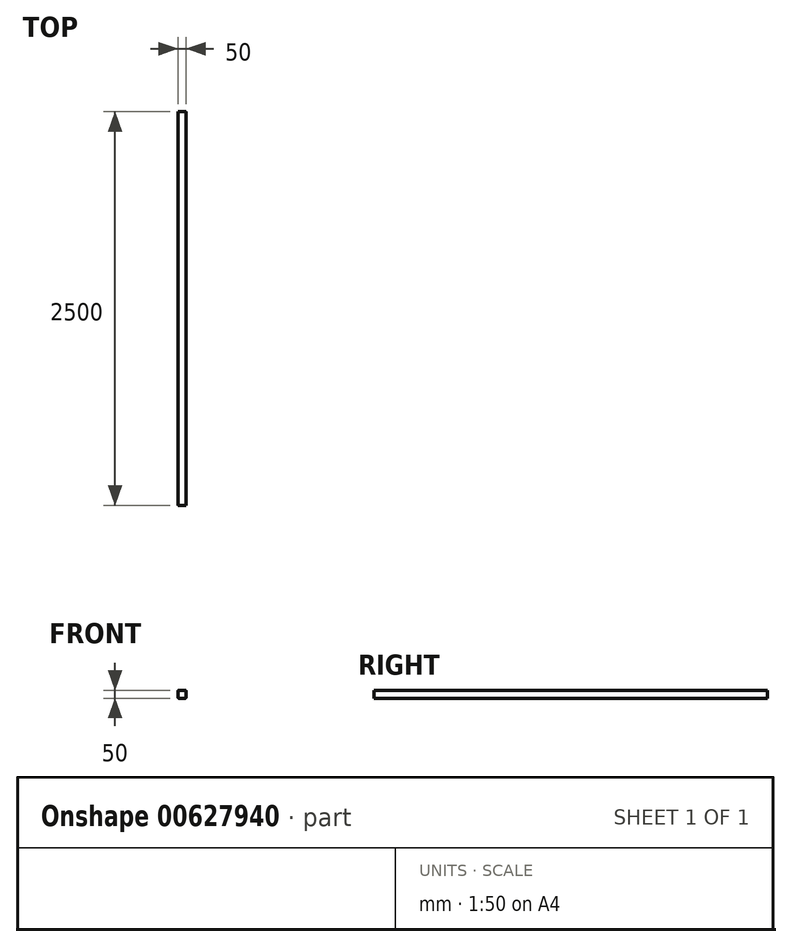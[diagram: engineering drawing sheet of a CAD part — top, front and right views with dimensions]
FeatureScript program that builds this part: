
annotation { "Feature Type Name" : "Feature", "Feature Type Description" : "" }
export const myFeature = defineFeature(function(context is Context, id is Id, definition is map)
    precondition{}
    {
        {
            var Q0;
            Q0=qCreatedBy(makeId("Front.planeOp"),FACE);
            var sketch = newSketch(context, id + "F0", { "sketchPlane" : qUnion([Q0])});
            skLineSegment(sketch, "E0.bottom", {"start": v(-47, 50) * mm, "end": v(-3, 50) * mm});
            skLineSegment(sketch, "E0.top", {"start": v(-47, 0) * mm, "end": v(-3, 0) * mm});
            skLineSegment(sketch, "E0.left", {"start": v(-50, 47) * mm, "end": v(-50, 3) * mm});
            skLineSegment(sketch, "E0.right", {"start": v(0, 47) * mm, "end": v(0, 3) * mm});
            skPoint(sketch, "E1.visualSharp", {"position": v(-50, 50) * mm});
            skArc(sketch, "E1.filletArc", {"start": v(-47, 50) * mm, "mid": v(-49.12, 49.12) * mm, "end": v(-50, 47) * mm});
            skPoint(sketch, "E2.visualSharp", {"position": v(0, 50) * mm});
            skArc(sketch, "E2.filletArc", {"start": v(0, 47) * mm, "mid": v(-0.88, 49.12) * mm, "end": v(-3, 50) * mm});
            skPoint(sketch, "E3.visualSharp", {"position": v(0, 0) * mm});
            skArc(sketch, "E3.filletArc", {"start": v(-3, 0) * mm, "mid": v(-0.88, 0.88) * mm, "end": v(0, 3) * mm});
            skPoint(sketch, "E4.visualSharp", {"position": v(-50, 0) * mm});
            skArc(sketch, "E4.filletArc", {"start": v(-50, 3) * mm, "mid": v(-49.12, 0.88) * mm, "end": v(-47, 0) * mm});
            skSolve(sketch);
        }
        {
            var Q0;
            Q0 = qSketchRegion(id + "F0", true);
            extrude(context, id + "F1", {"entities" : qUnion([Q0]), "depth" : 2500 * mm, "offsetDistance" : 25 * mm});
        }
    });
